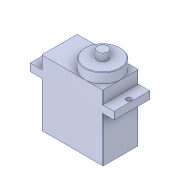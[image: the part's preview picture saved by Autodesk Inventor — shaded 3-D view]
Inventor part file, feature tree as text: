
AUTODESK INVENTOR PART (.ipt)
format: ipt  version: 2019 (Build 230136000, 136)  size: 156,160 bytes
history: mixed  units: in
note: dims shown in document units (in); Inventor stores cm internally (conversion verified against a paired STEP export)
features: fillet x1, imported_body x1
ambient origin geometry x8: Origin, YZ Plane, XZ Plane, XY Plane, X Axis, Y Axis, Z Axis, Center Point
bodies: Solid1 (imported_parasolid)
feature tree (2):
  fillet  "Fillet2"  [1 undecoded]
  imported_body  NMx_Import_Brep_tag  [imported B-rep: ~36 faces, bbox_mm=[33.0, 33.0, 14.0]]
note: 1 required parameter value undecoded (feature->parameter linkage not recoverable at this tier; creation-order binding heuristic only, values carry confidence <= 0.55)
